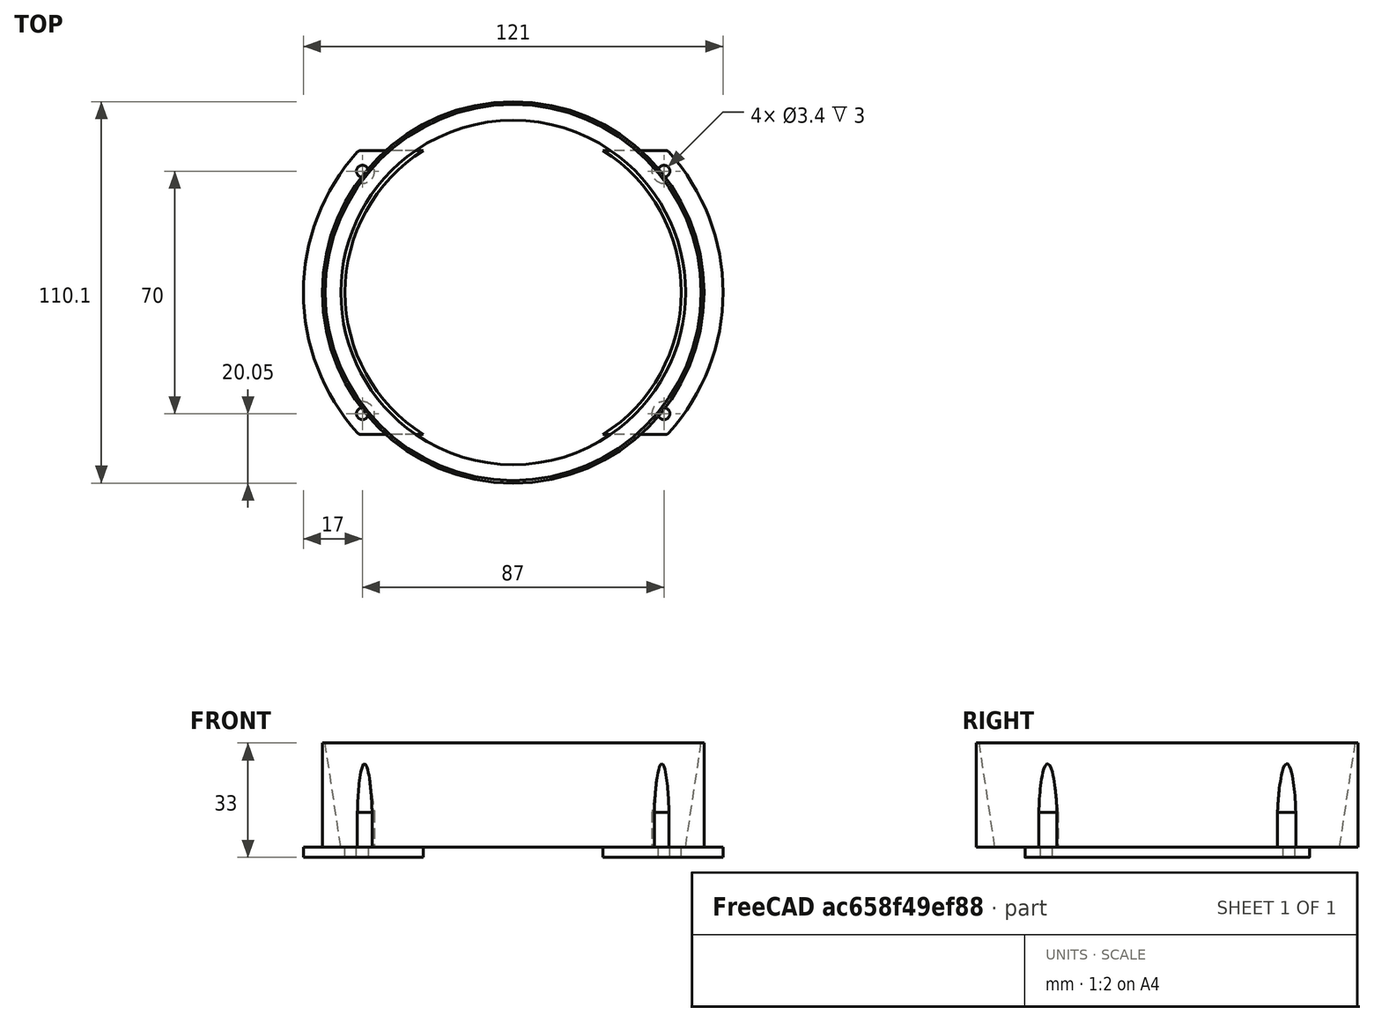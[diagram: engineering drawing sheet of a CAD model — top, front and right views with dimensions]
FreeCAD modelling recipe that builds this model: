
FCSTD DOCUMENT  (FreeCAD 0.19R24291 (Git))
Label: Крепление для стаканов
License: All rights reserved
LicenseURL: http://en.wikipedia.org/wiki/All_rights_reserved
objects: Sketcher::SketchObject×7, PartDesign::Pocket×3, PartDesign::Mirrored×3, Mesh::Feature×1, PartDesign::Revolution×1, PartDesign::Pad×1, Spreadsheet::Sheet×1, PartDesign::SubtractiveLoft×1, PartDesign::MultiTransform×1, PartDesign::Body×1
note: 24 computed .brp shape members not serialized (recipe doc carries the construction recipe); baked Part::Feature solids carry a one-line shape summary decoded from their .brp

FEATURE [Mesh::Feature] __________________________________________  label="Крепление для стаканов"
FEATURE [Sketcher::SketchObject] Sketch
  FullyConstrained = true
  MapMode = 5
  Placement = pos=(0,0,0) rot=(1,0,0;1.5708rad)
  Support = -> [XZ_Plane]
  sketch-geometry (4):
    g0: LineSegment StartX=49.25 StartY=0 StartZ=0 EndX=54.25 EndY=33 EndZ=0
    g1: LineSegment StartX=49.25 StartY=0 StartZ=0 EndX=55.05 EndY=0 EndZ=0
    g2: LineSegment StartX=54.25 StartY=33 StartZ=0 EndX=55.05 EndY=33 EndZ=0
    g3: LineSegment StartX=55.05 StartY=33 StartZ=0 EndX=55.05 EndY=0 EndZ=0
  constraints (12):
    c: PointOnObject(g0,g-1)
    c: PointOnObject(g1,g-1)
    c: Distance(g0,g-2) = 49.25
    c: DistanceX(g0,g0) = 5
    c: Coincident(g1,g0)
    c: Coincident(g2,g0)
    c: Horizontal(g2)
    c: Coincident(g3,g2)
    c: Coincident(g3,g1)
    c: Vertical(g3)
    c: Distance(g2) = 0.8
    c: Distance(g3) = 33
FEATURE [PartDesign::Revolution] Revolution
  Angle = 360
  Axis = (0,2e-16,1)
  Base = (0,0,0)
  Placement = pos=(0,0,0) rot=(1,0,0;1.5708rad)
  Profile = -> Sketch
  ReferenceAxis = -> Sketch [V_Axis]
  Reversed = true
FEATURE [Sketcher::SketchObject] Sketch001
  FullyConstrained = false
  MapMode = 5
  Placement = pos=(0,0,0) rot=(0.57735,0.57735,0.57735;2.0944rad)
  Support = -> [YZ_Plane]
  sketch-geometry (4):
    g0: LineSegment StartX=41 StartY=0 StartZ=0 EndX=56.3222 EndY=0 EndZ=0
    g1: LineSegment StartX=56.3222 StartY=0 StartZ=0 EndX=56.3222 EndY=3 EndZ=0
    g2: LineSegment StartX=56.3222 StartY=3 StartZ=0 EndX=41 EndY=3 EndZ=0
    g3: LineSegment StartX=41 StartY=3 StartZ=0 EndX=41 EndY=0 EndZ=0
  constraints (11):
    c: Coincident(g0,g1)
    c: Coincident(g1,g2)
    c: Coincident(g2,g3)
    c: Coincident(g3,g0)
    c: Horizontal(g0)
    c: Horizontal(g2)
    c: Vertical(g1)
    c: Vertical(g3)
    c: PointOnObject(g0,g-1)
    c: Distance(g1) = 3
    c: Distance(g0,g-2) = 41
FEATURE [PartDesign::Pocket] Pocket
  BaseFeature = -> Revolution
  Length = 5
  Length2 = 100
  Midplane = true
  Placement = pos=(0,0,0) rot=(1,0,0;1.5708rad)
  Profile = -> Sketch001
  Type = 1
FEATURE [PartDesign::Mirrored] Mirrored
  BaseFeature = -> Pocket
  MirrorPlane = -> Sketch001 [V_Axis]
  Originals = -> [Pocket]
  Placement = pos=(0,0,0) rot=(1,0,0;1.5708rad)
FEATURE [Sketcher::SketchObject] Sketch002
  FullyConstrained = true
  MapMode = 5
  Support = -> [XY_Plane]
  sketch-geometry (5):
    g0: ArcOfCircle CenterX=0 CenterY=0 CenterZ=0 NormalX=0 NormalY=0 NormalZ=1 AngleXU=0 Radius=60.5 StartAngle=0 EndAngle=0.733524
    g1: ArcOfCircle CenterX=43.8264 CenterY=39.5 CenterZ=0 NormalX=0 NormalY=0 NormalZ=1 AngleXU=0 Radius=1.5 StartAngle=0.733524 EndAngle=1.5708
    g2: LineSegment StartX=25.9085 StartY=41 StartZ=0 EndX=43.8264 EndY=41 EndZ=0
    g3: LineSegment StartX=48.5 StartY=0 StartZ=0 EndX=60.5 EndY=0 EndZ=0
    g4: ArcOfCircle CenterX=0 CenterY=0 CenterZ=0 NormalX=0 NormalY=0 NormalZ=1 AngleXU=0 Radius=48.5 StartAngle=0 EndAngle=1.00724
  constraints (16):
    c: Coincident(g0,g-1)
    c: PointOnObject(g0,g-1)
    c: PointOnObject(g3,g-1)
    c: Coincident(g1,g0)
    c: Coincident(g2,g1)
    c: Horizontal(g2)
    c: Coincident(g3,g0)
    c: Diameter(g0) = 121
    c: Tangent(g0,g1)
    c: Tangent(g1,g2)
    c: Distance(g2,g-1) = 41
    c: Diameter(g1) = 3
    c: Coincident(g4,g0)
    c: Diameter(g4) = 97
    c: Coincident(g2,g4)
    c: Coincident(g4,g3)
FEATURE [PartDesign::Pad] Pad
  BaseFeature = -> Mirrored
  Direction = (1,1,1)
  Length = 3
  Length2 = 100
  Placement = pos=(0,0,0) rot=(1,0,0;1.5708rad)
  Profile = -> Sketch002
  Type = 0
FEATURE [Sketcher::SketchObject] Sketch003
  AttachmentOffset = pos=(0,0,3) rot=(0,0,1;0rad)
  FullyConstrained = true
  MapMode = 5
  Placement = pos=(0,0,3) rot=(0,0,1;0rad)
  Support = -> [XY_Plane]
  sketch-geometry (1):
    g0: Circle CenterX=43.5 CenterY=35 CenterZ=0 NormalX=0 NormalY=0 NormalZ=1 AngleXU=0 Radius=3.5
  constraints (3):
    c: Diameter(g0) = 7
    c: DistanceX(g0) = 43.5
    c: DistanceY(g0) = 35
FEATURE [PartDesign::Pocket] Pocket001
  BaseFeature = -> Pad
  Length = 10
  Length2 = 100
  Placement = pos=(0,0,0) rot=(1,0,0;1.5708rad)
  Profile = -> Sketch003
  Reversed = true
  Type = 0
FEATURE [Sketcher::SketchObject] Sketch004
  FullyConstrained = true
  MapMode = 5
  Support = -> [XY_Plane]
  sketch-geometry (1):
    g0: Circle CenterX=43.5 CenterY=35 CenterZ=0 NormalX=0 NormalY=0 NormalZ=1 AngleXU=0 Radius=1.7
  constraints (3):
    c: Diameter(g0) = 3.4
    c: DistanceX(g0) = 43.5
    c: DistanceY(g0) = 35
FEATURE [PartDesign::Pocket] Pocket002
  BaseFeature = -> Pocket001
  Length = 5
  Length2 = 100
  Placement = pos=(0,0,0) rot=(1,0,0;1.5708rad)
  Profile = -> Sketch004
  Reversed = true
  Type = 0
FEATURE [Sketcher::SketchObject] Sketch005
  AttachmentOffset = pos=(0,0,13) rot=(0,0,1;0rad)
  FullyConstrained = true
  MapMode = 5
  Placement = pos=(0,0,13) rot=(0,0,1;0rad)
  Support = -> [XY_Plane]
  sketch-geometry (1):
    g0: Circle CenterX=43.5 CenterY=35 CenterZ=0 NormalX=0 NormalY=0 NormalZ=1 AngleXU=0 Radius=3.5
  constraints (3):
    c: Diameter(g0) = 7
    c: DistanceX(g0) = 43.5
    c: DistanceY(g0) = 35
FEATURE [Sketcher::SketchObject] Sketch006
  AttachmentOffset = pos=(0,0,43) rot=(0,0,1;0rad)
  FullyConstrained = true
  MapMode = 5
  Placement = pos=(0,0,43) rot=(0,0,1;0rad)
  Support = -> [XY_Plane]
  expr: .AttachmentOffset.Base.z = Spreadsheet.height + 10
  sketch-geometry (3):
    g0: LineSegment StartX=0 StartY=0 StartZ=0 EndX=48.0189 EndY=38.6359 EndZ=0
    g1: GeomPoint X=43.5 Y=35 Z=0
    g2: Circle CenterX=48.0189 CenterY=38.6359 CenterZ=0 NormalX=0 NormalY=0 NormalZ=1 AngleXU=0 Radius=3.5
  constraints (7):
    c: Coincident(g0,g-1)
    c: PointOnObject(g1,g0)
    c: DistanceX(g1) = 43.5
    c: DistanceY(g1) = 35
    c: Distance(g1,g0) = 5.8
    c: Coincident(g2,g0)
    c: Diameter(g2) = 7
FEATURE [Spreadsheet::Sheet] Spreadsheet
  cells = B3(height)=33; B4(rotation_max_thickness)=5.8
FEATURE [PartDesign::SubtractiveLoft] SubtractiveLoft
  BaseFeature = -> Pocket002
  Closed = false
  Placement = pos=(0,0,0) rot=(1,0,0;1.5708rad)
  Profile = -> Sketch005
  Ruled = false
  Sections = -> [Sketch006]
FEATURE [PartDesign::Mirrored] Mirrored001
  MirrorPlane = -> Sketch002 [V_Axis]
  Placement = pos=(0,0,0) rot=(1,0,0;1.5708rad)
FEATURE [PartDesign::Mirrored] Mirrored002
  MirrorPlane = -> Sketch002 [H_Axis]
  Placement = pos=(0,0,0) rot=(1,0,0;1.5708rad)
FEATURE [PartDesign::MultiTransform] MultiTransform
  BaseFeature = -> SubtractiveLoft
  Originals = -> [Pad,Pocket001,Pocket002,SubtractiveLoft]
  Placement = pos=(0,0,0) rot=(1,0,0;1.5708rad)
  Transformations = -> [Mirrored001,Mirrored002]
FEATURE [PartDesign::Body] Body
  Group = -> [Sketch,Revolution,Sketch001,Pocket,Mirrored,Sketch002,Pad,Sketch003,Pocket001,Sketch004,Pocket002,Sketch005,Sketch006,SubtractiveLoft,MultiTransform,Mirrored001,Mirrored002]
  Origin = -> Origin
  Tip = -> MultiTransform
